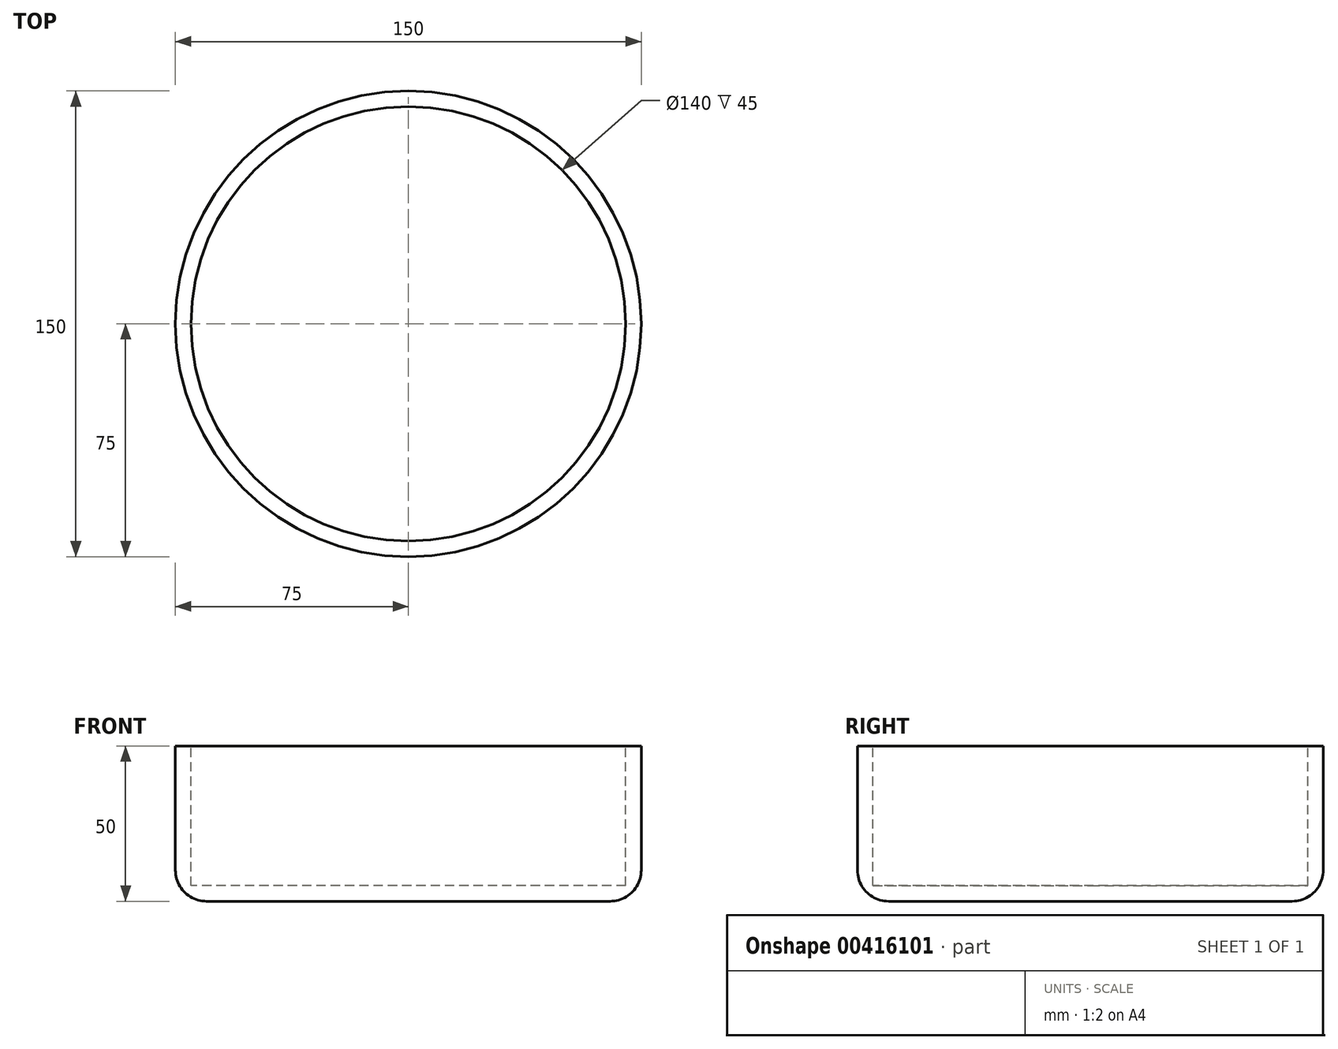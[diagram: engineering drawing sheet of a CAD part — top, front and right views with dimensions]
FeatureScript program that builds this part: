
annotation { "Feature Type Name" : "Feature", "Feature Type Description" : "" }
export const myFeature = defineFeature(function(context is Context, id is Id, definition is map)
    precondition{}
    {
        {
            var Q0;
            Q0=qCreatedBy(makeId("Top.planeOp"),FACE);
            var sketch = newSketch(context, id + "F0", { "sketchPlane" : qUnion([Q0])});
            skCircle(sketch, "E0", {"center": v(0, 0) * mm, "radius": 75 * mm});
            skSolve(sketch);
        }
        {
            var Q0;
            Q0=makeQuery(id+"F0.imprint","IMPRINT",FACE,{"disambiguationData":[TD([[makeQuery(id+"F0.imprint","IMPRINT",EDGE,{"derivedFrom":sQuery(id+"F0.wireOp",EDGE,"E0")}),1.0]])]});
            var Q1;
            Q1=sQuery(id+"F0.wireOp",EDGE,"E0");
            extrude(context, id + "F1", {"entities" : qUnion([Q0]), "surfaceEntities" : qUnion([Q1]), "oppositeDirection" : true, "depth" : 50 * mm});
        }
        {
            var Q0;
            Q0=makeQuery(id+"F1.opExtrude","CAP_FACE",FACE,{"disambiguationData":[OSD([sQuery(id+"F0.wireOp",EDGE,"E0")])],"isStart":true});
            var sketch = newSketch(context, id + "F2", { "sketchPlane" : qUnion([Q0])});
            skCircle(sketch, "E1.0", {"center": v(0, 0) * mm, "radius": 70 * mm});
            skSolve(sketch);
        }
        {
            var Q0;
            Q0=makeQuery(id+"F2.imprint","IMPRINT",FACE,{"disambiguationData":[TD([[makeQuery(id+"F2.imprint","IMPRINT",EDGE,{"derivedFrom":sQuery(id+"F2.wireOp",EDGE,"E1.0")}),1.0]])]});
            var Q1;
            Q1=sQuery(id+"F2.wireOp",EDGE,"E1.0");
            extrude(context, id + "F3", {"entities" : qUnion([Q0]), "operationType" : NewBodyOperationType.REMOVE, "surfaceEntities" : qUnion([Q1]), "oppositeDirection" : true, "depth" : 45 * mm});
        }
        {
            var Q0;
            Q0=makeQuery(id+"F1.opExtrude","CAP_EDGE",EDGE,{"disambiguationData":[OSD([sQuery(id+"F0.wireOp",EDGE,"E0")])],"isStart":false});
            fillet(context, id + "F4", {"entities" : qUnion([Q0]), "radius" : 10 * mm, "tangentPropagation" : true, "allowEdgeOverflow" : false});
        }
    });
